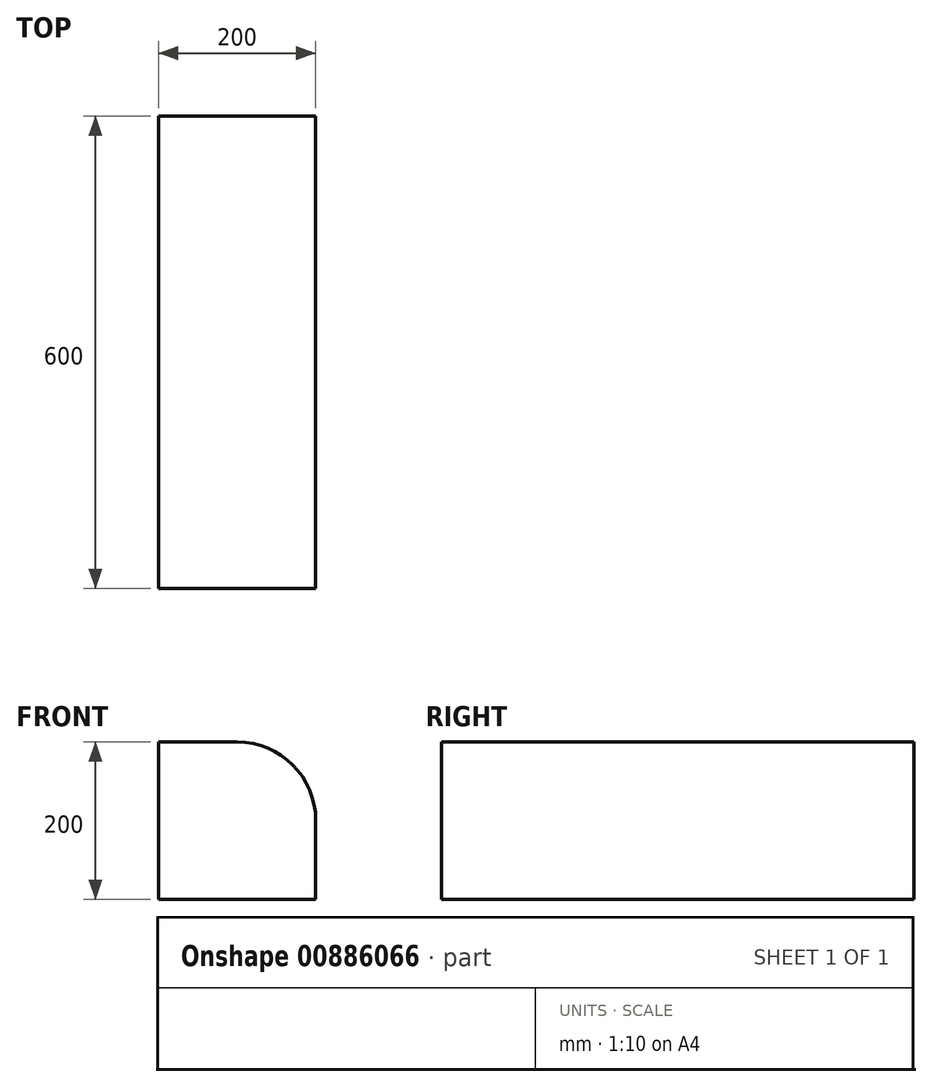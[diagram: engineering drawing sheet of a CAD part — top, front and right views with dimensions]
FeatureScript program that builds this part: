
annotation { "Feature Type Name" : "Feature", "Feature Type Description" : "" }
export const myFeature = defineFeature(function(context is Context, id is Id, definition is map)
    precondition{}
    {
        {
            var Q0;
            Q0=qCreatedBy(makeId("Front.planeOp"),FACE);
            var sketch = newSketch(context, id + "F0", { "sketchPlane" : qUnion([Q0])});
            skLineSegment(sketch, "E0.bottom", {"start": v(0, 0) * mm, "end": v(100, 0) * mm});
            skLineSegment(sketch, "E0.top", {"start": v(0, -200) * mm, "end": v(200, -200) * mm});
            skLineSegment(sketch, "E0.left", {"start": v(0, 0) * mm, "end": v(0, -200) * mm});
            skLineSegment(sketch, "E0.right", {"start": v(200, -100) * mm, "end": v(200, -200) * mm});
            skPoint(sketch, "E1.visualSharp", {"position": v(200, 0) * mm});
            skArc(sketch, "E1.filletArc", {"start": v(200, -100) * mm, "mid": v(170.71, -29.29) * mm, "end": v(100, 0) * mm});
            skSolve(sketch);
        }
        {
            var Q0;
            Q0=makeQuery(id+"F0.imprint","IMPRINT",FACE,{"disambiguationData":[TD([[makeQuery(id+"F0.imprint","IMPRINT",EDGE,{"derivedFrom":sQuery(id+"F0.wireOp",EDGE,"E0.bottom")}),-1.0]])]});
            extrude(context, id + "F1", {"entities" : qUnion([Q0]), "endBound" : BoundingType.SYMMETRIC, "oppositeDirection" : true, "depth" : 600 * mm, "offsetDistance" : 25 * mm});
        }
    });
